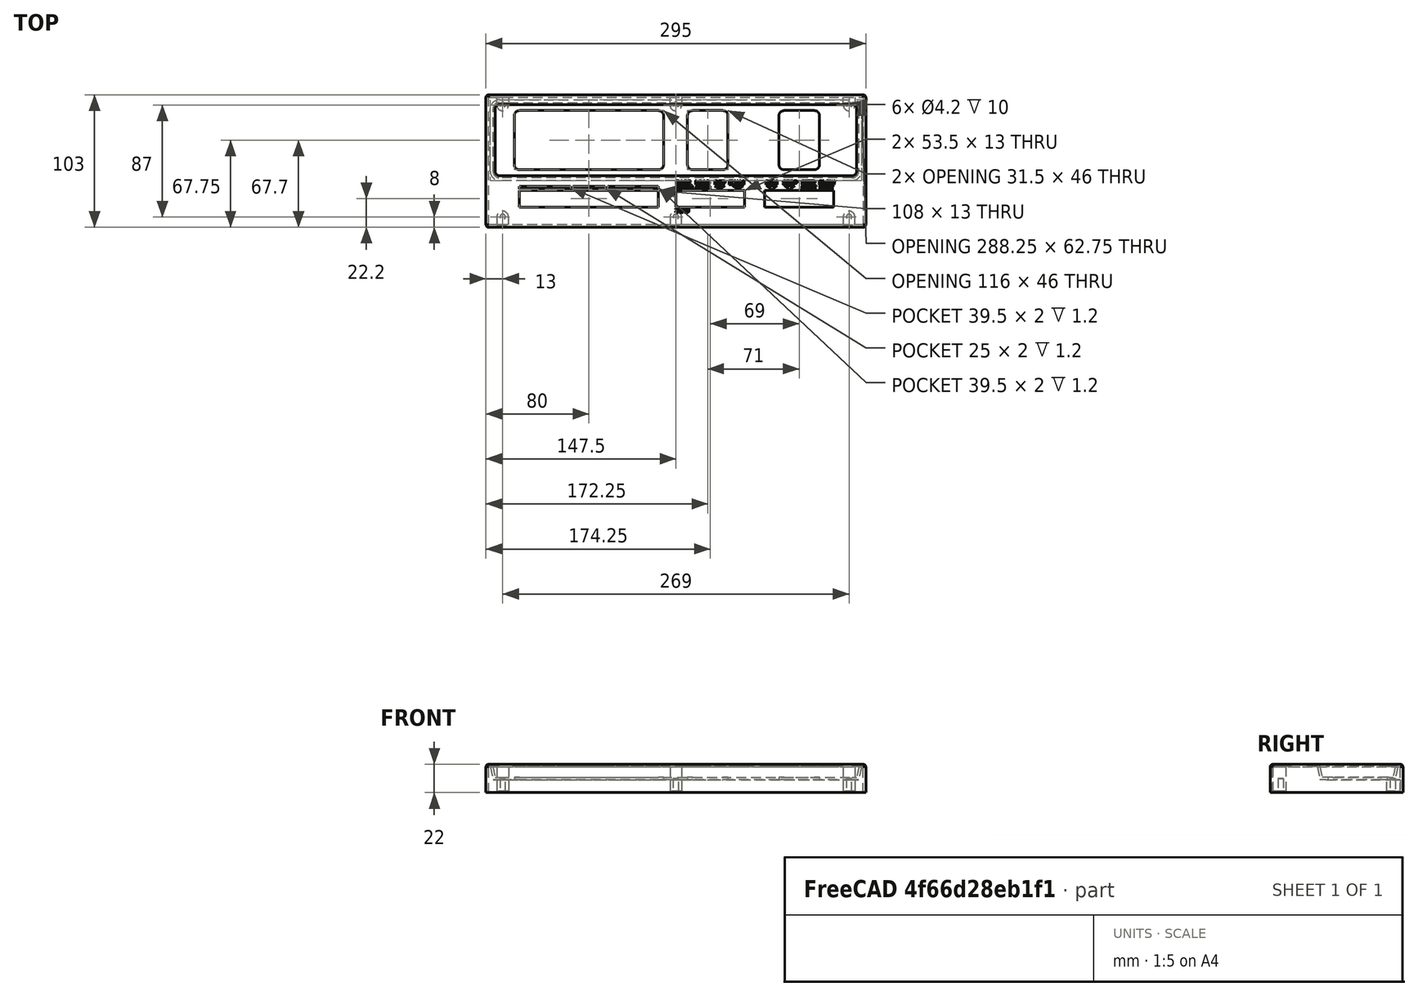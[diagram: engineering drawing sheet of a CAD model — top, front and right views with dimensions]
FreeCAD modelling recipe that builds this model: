
FCSTD DOCUMENT  (FreeCAD 1.0R39109 (Git))
Label: front panel
License: All rights reserved
LicenseURL: http://en.wikipedia.org/wiki/All_rights_reserved
objects: PartDesign::Pocket×17, Part::Part2DObjectPython×13, Sketcher::SketchObject×7, PartDesign::LinearPattern×4, PartDesign::Pad×3, PartDesign::Draft×1, PartDesign::Thickness×1, PartDesign::MultiTransform×1, PartDesign::Body×1, TechDraw::DrawSVGTemplate×1, TechDraw::DrawProjGroupItem×1, TechDraw::DrawProjGroup×1, TechDraw::DrawViewDimension×1, TechDraw::DrawPage×1, Mesh::Feature×1
note: 106 computed .brp shape members not serialized (recipe doc carries the construction recipe); baked Part::Feature solids carry a one-line shape summary decoded from their .brp

FEATURE [Sketcher::SketchObject] Sketch
  ArcFitTolerance = 0
  AttachmentSupport = -> [XY_Plane]
  FullyConstrained = true
  MakeInternals = false
  MapMode = 5
  sketch-geometry (4):
    g0: LineSegment StartX=-145.5 StartY=49.5 StartZ=0 EndX=145.5 EndY=49.5 EndZ=0
    g1: LineSegment StartX=145.5 StartY=49.5 StartZ=0 EndX=145.5 EndY=-49.5 EndZ=0
    g2: LineSegment StartX=145.5 StartY=-49.5 StartZ=0 EndX=-145.5 EndY=-49.5 EndZ=0
    g3: LineSegment StartX=-145.5 StartY=-49.5 StartZ=0 EndX=-145.5 EndY=49.5 EndZ=0
  constraints (11):
    c: Coincident(g0,g1)
    c: Coincident(g1,g2)
    c: Coincident(g2,g3)
    c: Coincident(g3,g0)
    c: Horizontal(g0)
    c: Horizontal(g2)
    c: Vertical(g1)
    c: Vertical(g3)
    c: Symmetric(g1,g0,g-1)
    c: DistanceY(g3,g3) = 99
    c: DistanceX(g0,g0) = 291
FEATURE [PartDesign::Pad] Pad
  Direction = (0,0,1)
  Length = 20
  Length2 = 10
  Profile = -> Sketch
  ReferenceAxis = -> Sketch [N_Axis]
  Suppressed = false
  Type = 0
FEATURE [Sketcher::SketchObject] Sketch001
  ArcFitTolerance = 0
  AttachmentSupport = -> [Pad]
  FullyConstrained = true
  MakeInternals = false
  MapMode = 5
  Placement = pos=(0,0,20) rot=(0,0,1;0rad)
  sketch-geometry (10):
    g0: ArcOfCircle CenterX=-137 CenterY=40.5 CenterZ=0 NormalX=0 NormalY=0 NormalZ=1 AngleXU=0 Radius=5 StartAngle=1.5708 EndAngle=3.14159
    g1: LineSegment StartX=-137 StartY=45.5 StartZ=0 EndX=137 EndY=45.5 EndZ=0
    g2: ArcOfCircle CenterX=137 CenterY=40.5 CenterZ=0 NormalX=0 NormalY=0 NormalZ=1 AngleXU=0 Radius=5 StartAngle=5e-16 EndAngle=1.5708
    g3: LineSegment StartX=142 StartY=40.5 StartZ=0 EndX=142 EndY=-8 EndZ=0
    g4: ArcOfCircle CenterX=137 CenterY=-8 CenterZ=0 NormalX=0 NormalY=0 NormalZ=1 AngleXU=0 Radius=5 StartAngle=4.71239 EndAngle=6.28319
    g5: LineSegment StartX=137 StartY=-13 StartZ=0 EndX=-137 EndY=-13 EndZ=0
    g6: ArcOfCircle CenterX=-137 CenterY=-8 CenterZ=0 NormalX=0 NormalY=0 NormalZ=1 AngleXU=0 Radius=5 StartAngle=3.14159 EndAngle=4.71239
    g7: LineSegment StartX=-142 StartY=-8 StartZ=0 EndX=-142 EndY=40.5 EndZ=0
    g8: GeomPoint [constr] X=-142 Y=45.5 Z=0
    g9: GeomPoint [constr] X=142 Y=-13 Z=0
  constraints (23):
    c: Tangent(g0,g1) = 1.5708
    c: Tangent(g1,g2) = 1.5708
    c: Tangent(g2,g3) = 1.5708
    c: Tangent(g3,g4) = 1.5708
    c: Tangent(g4,g5) = 1.5708
    c: Tangent(g5,g6) = 1.5708
    c: Tangent(g6,g7) = 1.5708
    c: Tangent(g7,g0) = 1.5708
    c: Horizontal(g1)
    c: Horizontal(g5)
    c: Vertical(g3)
    c: Vertical(g7)
    c: Equal(g2,g4)
    c: Equal(g4,g6)
    c: PointOnObject(g8,g1)
    c: PointOnObject(g8,g7)
    c: PointOnObject(g9,g3)
    c: PointOnObject(g9,g5)
    c: Diameter(g2) = 10
    c: DistanceX(g0,g2) = 284
    c: Symmetric(g0,g2,g-2)
    c: DistanceY(g-1,g0) = 45.5
    c: DistanceY(g5,g-1) = 13
FEATURE [PartDesign::Pocket] Pocket
  BaseFeature = -> Pad
  Direction = (0,0,-1)
  Length = 10
  Length2 = 5
  Profile = -> Sketch001
  ReferenceAxis = -> Sketch001 [N_Axis]
  Suppressed = false
  Type = 0
FEATURE [PartDesign::Draft] Draft
  Angle = 12
  Base = -> Pocket [Face10]
  BaseFeature = -> Pocket
  NeutralPlane = -> Pocket [Face15]
  SupportTransform = false
  Suppressed = false
FEATURE [PartDesign::Thickness] Thickness
  Base = -> Draft [Face4]
  BaseFeature = -> Draft
  Intersection = false
  Join = 0
  Mode = 0
  SupportTransform = false
  Suppressed = false
  Value = 2
FEATURE [Sketcher::SketchObject] Sketch002
  ArcFitTolerance = 0
  AttachmentSupport = -> [Thickness]
  FullyConstrained = true
  MakeInternals = false
  MapMode = 5
  Placement = pos=(0,0,22) rot=(0,0,1;0rad)
  sketch-geometry (42):
    g0: LineSegment StartX=-121.5 StartY=-22.8 StartZ=0 EndX=-13.5 EndY=-22.8 EndZ=0
    g1: LineSegment StartX=-13.5 StartY=-22.8 StartZ=0 EndX=-13.5 EndY=-35.8 EndZ=0
    g2: LineSegment StartX=-13.5 StartY=-35.8 StartZ=0 EndX=-121.5 EndY=-35.8 EndZ=0
    g3: LineSegment StartX=-121.5 StartY=-35.8 StartZ=0 EndX=-121.5 EndY=-22.8 EndZ=0
    g4: LineSegment StartX=0 StartY=-22.8 StartZ=0 EndX=53.5 EndY=-22.8 EndZ=0
    g5: LineSegment StartX=53.5 StartY=-22.8 StartZ=0 EndX=53.5 EndY=-35.8 EndZ=0
    g6: LineSegment StartX=53.5 StartY=-35.8 StartZ=0 EndX=0 EndY=-35.8 EndZ=0
    g7: LineSegment StartX=0 StartY=-35.8 StartZ=0 EndX=0 EndY=-22.8 EndZ=0
    g8: LineSegment StartX=69 StartY=-22.8 StartZ=0 EndX=122.5 EndY=-22.8 EndZ=0
    g9: LineSegment StartX=122.5 StartY=-22.8 StartZ=0 EndX=122.5 EndY=-35.8 EndZ=0
    g10: LineSegment StartX=122.5 StartY=-35.8 StartZ=0 EndX=69 EndY=-35.8 EndZ=0
    g11: LineSegment StartX=69 StartY=-35.8 StartZ=0 EndX=69 EndY=-22.8 EndZ=0
    g12: ArcOfCircle CenterX=-121.5 CenterY=35.2 CenterZ=0 NormalX=0 NormalY=0 NormalZ=1 AngleXU=0 Radius=4 StartAngle=1.5708 EndAngle=3.14159
    g13: LineSegment StartX=-121.5 StartY=39.2 StartZ=0 EndX=-13.5 EndY=39.2 EndZ=0
    g14: ArcOfCircle CenterX=-13.5 CenterY=35.2 CenterZ=0 NormalX=0 NormalY=0 NormalZ=1 AngleXU=0 Radius=4 StartAngle=-9e-16 EndAngle=1.5708
    g15: LineSegment StartX=-9.5 StartY=35.2 StartZ=0 EndX=-9.5 EndY=-2.8 EndZ=0
    g16: ArcOfCircle CenterX=-13.5 CenterY=-2.8 CenterZ=0 NormalX=0 NormalY=0 NormalZ=1 AngleXU=0 Radius=4 StartAngle=4.71239 EndAngle=6.28319
    g17: LineSegment StartX=-13.5 StartY=-6.8 StartZ=0 EndX=-121.5 EndY=-6.8 EndZ=0
    g18: ArcOfCircle CenterX=-121.5 CenterY=-2.8 CenterZ=0 NormalX=0 NormalY=0 NormalZ=1 AngleXU=0 Radius=4 StartAngle=3.14159 EndAngle=4.71239
    g19: LineSegment StartX=-125.5 StartY=-2.8 StartZ=0 EndX=-125.5 EndY=35.2 EndZ=0
    g20: GeomPoint [constr] X=-125.5 Y=39.2 Z=0
    g21: GeomPoint [constr] X=-9.5 Y=-6.8 Z=0
    g22: ArcOfCircle CenterX=13 CenterY=35.2 CenterZ=0 NormalX=0 NormalY=0 NormalZ=1 AngleXU=0 Radius=4 StartAngle=1.5708 EndAngle=3.14159
    g23: LineSegment StartX=13 StartY=39.2 StartZ=0 EndX=36.5 EndY=39.2 EndZ=0
    g24: ArcOfCircle CenterX=36.5 CenterY=35.2 CenterZ=0 NormalX=0 NormalY=0 NormalZ=1 AngleXU=0 Radius=4 StartAngle=-9e-16 EndAngle=1.5708
    g25: LineSegment StartX=40.5 StartY=35.2 StartZ=0 EndX=40.5 EndY=-2.8 EndZ=0
    g26: ArcOfCircle CenterX=36.5 CenterY=-2.8 CenterZ=0 NormalX=0 NormalY=0 NormalZ=1 AngleXU=0 Radius=4 StartAngle=4.71239 EndAngle=6.28319
    g27: LineSegment StartX=36.5 StartY=-6.8 StartZ=0 EndX=13 EndY=-6.8 EndZ=0
    g28: ArcOfCircle CenterX=13 CenterY=-2.8 CenterZ=0 NormalX=0 NormalY=0 NormalZ=1 AngleXU=0 Radius=4 StartAngle=3.14159 EndAngle=4.71239
    g29: LineSegment StartX=9 StartY=-2.8 StartZ=0 EndX=9 EndY=35.2 EndZ=0
    g30: GeomPoint [constr] X=9 Y=39.2 Z=0
    g31: GeomPoint [constr] X=40.5 Y=-6.8 Z=0
    g32: ArcOfCircle CenterX=84 CenterY=35.2 CenterZ=0 NormalX=0 NormalY=0 NormalZ=1 AngleXU=0 Radius=4 StartAngle=1.5708 EndAngle=3.14159
    g33: LineSegment StartX=84 StartY=39.2 StartZ=0 EndX=107.5 EndY=39.2 EndZ=0
    g34: ArcOfCircle CenterX=107.5 CenterY=35.2 CenterZ=0 NormalX=0 NormalY=0 NormalZ=1 AngleXU=0 Radius=4 StartAngle=0 EndAngle=1.5708
    g35: LineSegment StartX=111.5 StartY=35.2 StartZ=0 EndX=111.5 EndY=-2.8 EndZ=0
    g36: ArcOfCircle CenterX=107.5 CenterY=-2.8 CenterZ=0 NormalX=0 NormalY=0 NormalZ=1 AngleXU=0 Radius=4 StartAngle=4.71239 EndAngle=6.28319
    g37: LineSegment StartX=107.5 StartY=-6.8 StartZ=0 EndX=84 EndY=-6.8 EndZ=0
    g38: ArcOfCircle CenterX=84 CenterY=-2.8 CenterZ=0 NormalX=0 NormalY=0 NormalZ=1 AngleXU=0 Radius=4 StartAngle=3.14159 EndAngle=4.71239
    g39: LineSegment StartX=80 StartY=-2.8 StartZ=0 EndX=80 EndY=35.2 EndZ=0
    g40: GeomPoint [constr] X=80 Y=39.2 Z=0
    g41: GeomPoint [constr] X=111.5 Y=-6.8 Z=0
  constraints (108):
    c: Coincident(g0,g1)
    c: Coincident(g1,g2)
    c: Coincident(g2,g3)
    c: Coincident(g3,g0)
    c: Horizontal(g0)
    c: Horizontal(g2)
    c: Vertical(g1)
    c: Vertical(g3)
    c: Coincident(g4,g5)
    c: Coincident(g5,g6)
    c: Coincident(g6,g7)
    c: Coincident(g7,g4)
    c: Horizontal(g4)
    c: Horizontal(g6)
    c: Vertical(g5)
    c: Vertical(g7)
    c: Coincident(g8,g9)
    c: Coincident(g9,g10)
    c: Coincident(g10,g11)
    c: Coincident(g11,g8)
    c: Horizontal(g8)
    c: Horizontal(g10)
    c: Vertical(g9)
    c: Vertical(g11)
    c: Horizontal(g10,g5)
    c: Horizontal(g5,g1)
    c: Horizontal(g4,g0)
    c: Horizontal(g0,g8)
    c: DistanceY(g3,g3) = 13
    c: DistanceX(g2,g-1) = 121.5
    c: DistanceX(g0,g0) = 108
    c: DistanceY(g1,g-1) = 35.8
    c: DistanceX(g0,g4) = 13.5
    c: DistanceX(g4,g4) = 53.5
    c: DistanceX(g4,g8) = 15.5
    c: Equal(g8,g4)
    c: Tangent(g12,g13) = 1.5708
    c: Tangent(g13,g14) = 1.5708
    c: Tangent(g14,g15) = 1.5708
    c: Tangent(g15,g16) = 1.5708
    c: Tangent(g16,g17) = 1.5708
    c: Tangent(g17,g18) = 1.5708
    c: Tangent(g18,g19) = 1.5708
    c: Tangent(g19,g12) = 1.5708
    c: Horizontal(g13)
    c: Horizontal(g17)
    c: Vertical(g15)
    c: Vertical(g19)
    c: Equal(g12,g14)
    c: Equal(g14,g16)
    c: Equal(g16,g18)
    c: PointOnObject(g20,g13)
    c: PointOnObject(g20,g19)
    c: PointOnObject(g21,g15)
    c: PointOnObject(g21,g17)
    c: Radius(g12) = 4
    c: Vertical(g17,g0)
    c: Vertical(g16,g0)
    c: Tangent(g22,g23) = 1.5708
    c: Tangent(g23,g24) = 1.5708
    c: Tangent(g24,g25) = 1.5708
    c: Tangent(g25,g26) = 1.5708
    c: Tangent(g26,g27) = 1.5708
    c: Tangent(g27,g28) = 1.5708
    c: Tangent(g28,g29) = 1.5708
    c: Tangent(g29,g22) = 1.5708
    c: Horizontal(g23)
    c: Horizontal(g27)
    c: Vertical(g25)
    c: Vertical(g29)
    c: Equal(g22,g24)
    c: Equal(g24,g26)
    c: Equal(g26,g28)
    c: PointOnObject(g30,g23)
    c: PointOnObject(g30,g29)
    c: PointOnObject(g31,g25)
    c: PointOnObject(g31,g27)
    c: Equal(g26,g14)
    c: Horizontal(g22,g13)
    c: Horizontal(g27,g16)
    c: DistanceX(g26,g4) = 17
    c: DistanceX(g4,g27) = 13
    c: Tangent(g32,g33) = 1.5708
    c: Tangent(g33,g34) = 1.5708
    c: Tangent(g34,g35) = 1.5708
    c: Tangent(g35,g36) = 1.5708
    c: Tangent(g36,g37) = 1.5708
    c: Tangent(g37,g38) = 1.5708
    c: Tangent(g38,g39) = 1.5708
    c: Tangent(g39,g32) = 1.5708
    c: Horizontal(g33)
    c: Horizontal(g37)
    c: Vertical(g35)
    c: Vertical(g39)
    c: Equal(g32,g34)
    c: Equal(g34,g36)
    c: Equal(g36,g38)
    c: PointOnObject(g40,g33)
    c: PointOnObject(g40,g39)
    c: PointOnObject(g41,g35)
    c: PointOnObject(g41,g37)
    c: Horizontal(g23,g32)
    c: Equal(g32,g24)
    c: DistanceX(g36,g8) = 15
    c: DistanceY(g8,g35) = 20
    c: DistanceY(g8,g33) = 62
    c: Horizontal(g37,g16)
    c: Equal(g37,g27)
FEATURE [PartDesign::Pocket] Pocket001  label="Switch cut out"
  BaseFeature = -> Thickness
  Direction = (0,0,-1)
  Length = 5
  Length2 = 5
  Profile = -> Sketch002
  ReferenceAxis = -> Sketch002 [N_Axis]
  Suppressed = false
  Type = 1
FEATURE [Sketcher::SketchObject] Sketch003
  ArcFitTolerance = 0
  AttachmentSupport = -> [Pocket001]
  ExternalGeometry = -> [Pocket001]
  FullyConstrained = false
  MakeInternals = false
  MapMode = 5
  Placement = pos=(0,0,20) rot=(1,0,0;3.14159rad)
  sketch-geometry (5):
    g0: Circle [constr] CenterX=-134.5 CenterY=43.5 CenterZ=0 NormalX=0 NormalY=0 NormalZ=1 AngleXU=0 Radius=4.5
    g1: ArcOfCircle CenterX=-134.5 CenterY=43.5 CenterZ=0 NormalX=0 NormalY=0 NormalZ=1 AngleXU=0 Radius=4.5 StartAngle=3.14571 EndAngle=6.27841
    g2: LineSegment StartX=-139 StartY=43.4815 StartZ=0 EndX=-139.025 EndY=49.5 EndZ=0
    g3: LineSegment StartX=-139.025 StartY=49.5 StartZ=0 EndX=-130 EndY=49.5 EndZ=0
    g4: LineSegment StartX=-130 StartY=49.5 StartZ=0 EndX=-130 EndY=43.4785 EndZ=0
  constraints (12):
    c: DistanceY(g-1,g0) = 43.5
    c: DistanceX(g0,g-1) = 134.5
    c: Diameter(g0) = 9
    c: Coincident(g1,g0)
    c: PointOnObject(g1,g0)
    c: Tangent(g1,g2) = 1.5708
    c: Coincident(g2,g3)
    c: PointOnObject(g3,g-3)
    c: Horizontal(g3)
    c: Coincident(g3,g4)
    c: Coincident(g4,g1)
    c: Vertical(g4)
FEATURE [PartDesign::Pad] Pad001
  BaseFeature = -> Pocket001
  Direction = (0,0,-1)
  Length = 19
  Length2 = 10
  Profile = -> Sketch003
  ReferenceAxis = -> Sketch003 [N_Axis]
  Suppressed = false
  Type = 0
FEATURE [PartDesign::LinearPattern] LinearPattern
  BaseFeature = -> Pad001
  Direction = -> Sketch003 [H_Axis]
  Length = 269
  Mode = 0
  Occurrences = 3
  Offset = 134.5
  Originals = -> [Pad001]
  Suppressed = false
  TransformMode = 0
FEATURE [Sketcher::SketchObject] Sketch004
  ArcFitTolerance = 0
  AttachmentSupport = -> [LinearPattern]
  ExternalGeometry = -> [LinearPattern]
  FullyConstrained = true
  MakeInternals = false
  MapMode = 5
  Placement = pos=(0,0,10) rot=(1,0,0;3.14159rad)
  sketch-geometry (4):
    g0: ArcOfCircle CenterX=-134.5 CenterY=-43.5 CenterZ=0 NormalX=0 NormalY=0 NormalZ=1 AngleXU=0 Radius=4.5 StartAngle=-9e-16 EndAngle=3.14159
    g1: LineSegment StartX=-139 StartY=-43.5 StartZ=0 EndX=-139 EndY=-49.5 EndZ=0
    g2: LineSegment StartX=-139 StartY=-49.5 StartZ=0 EndX=-130 EndY=-49.5 EndZ=0
    g3: LineSegment StartX=-130 StartY=-49.5 StartZ=0 EndX=-130 EndY=-43.5 EndZ=0
  constraints (11):
    c: Tangent(g0,g1) = -1.5708
    c: Coincident(g1,g2)
    c: PointOnObject(g2,g-3)
    c: Horizontal(g2)
    c: Coincident(g2,g3)
    c: Vertical(g3)
    c: Vertical(g1)
    c: Diameter(g0) = 9
    c: DistanceX(g0,g-1) = 134.5
    c: DistanceY(g0,g-1) = 43.5
    c: Tangent(g3,g0) = -1.5708
FEATURE [PartDesign::Pad] Pad002
  BaseFeature = -> LinearPattern
  Direction = (0,0,-1)
  Length = 9
  Length2 = 10
  Profile = -> Sketch004
  ReferenceAxis = -> Sketch004 [N_Axis]
  Suppressed = false
  Type = 0
FEATURE [PartDesign::LinearPattern] LinearPattern001
  BaseFeature = -> Pad002
  Direction = -> Sketch004 [H_Axis]
  Length = 269
  Mode = 0
  Occurrences = 3
  Offset = 134.5
  Originals = -> [Pad002]
  Suppressed = false
  TransformMode = 0
FEATURE [Sketcher::SketchObject] Sketch005
  ArcFitTolerance = 0
  AttachmentSupport = -> [LinearPattern001]
  ExternalGeometry = -> [LinearPattern001]
  FullyConstrained = true
  MakeInternals = false
  MapMode = 5
  Placement = pos=(0,0,1) rot=(1,0,0;3.14159rad)
  sketch-geometry (1):
    g0: Circle CenterX=-134.5 CenterY=43.5 CenterZ=0 NormalX=0 NormalY=0 NormalZ=1 AngleXU=0 Radius=2.1
  constraints (2):
    c: Coincident(g0,g-3)
    c: Diameter(g0) = 4.2
FEATURE [PartDesign::Pocket] Pocket002
  BaseFeature = -> LinearPattern001
  Direction = (0,0,1)
  Length = 10
  Length2 = 5
  Profile = -> Sketch005
  ReferenceAxis = -> Sketch005 [N_Axis]
  Suppressed = false
  Type = 0
FEATURE [PartDesign::LinearPattern] LinearPattern002
  Direction = -> Sketch005 [H_Axis]
  Length = 269
  Mode = 0
  Occurrences = 3
  Offset = 134.5
  Suppressed = false
  TransformMode = 0
FEATURE [PartDesign::LinearPattern] LinearPattern003
  Direction = -> Sketch005 [V_Axis]
  Length = 87
  Mode = 0
  Occurrences = 2
  Offset = 87
  Reversed = true
  Suppressed = false
  TransformMode = 0
FEATURE [PartDesign::MultiTransform] MultiTransform
  BaseFeature = -> Pocket002
  Originals = -> [Pocket002]
  Suppressed = false
  TransformMode = 0
  Transformations = -> [LinearPattern002,LinearPattern003]
FEATURE [Sketcher::SketchObject] Sketch006
  ArcFitTolerance = 0
  AttachmentSupport = -> [MultiTransform]
  ExternalGeometry = -> [MultiTransform]
  FullyConstrained = true
  MakeInternals = false
  MapMode = 5
  Placement = pos=(0,0,22) rot=(0,0,1;0rad)
  sketch-geometry (28):
    g0: LineSegment StartX=-121.5 StartY=-19.8 StartZ=0 EndX=-82 EndY=-19.8 EndZ=0
    g1: LineSegment StartX=-82 StartY=-19.8 StartZ=0 EndX=-82 EndY=-21.8 EndZ=0
    g2: LineSegment StartX=-82 StartY=-21.8 StartZ=0 EndX=-121.5 EndY=-21.8 EndZ=0
    g3: LineSegment StartX=-121.5 StartY=-21.8 StartZ=0 EndX=-121.5 EndY=-19.8 EndZ=0
    g4: LineSegment StartX=-80 StartY=-19.8 StartZ=0 EndX=-55 EndY=-19.8 EndZ=0
    g5: LineSegment StartX=-55 StartY=-19.8 StartZ=0 EndX=-55 EndY=-21.8 EndZ=0
    g6: LineSegment StartX=-55 StartY=-21.8 StartZ=0 EndX=-80 EndY=-21.8 EndZ=0
    g7: LineSegment StartX=-80 StartY=-21.8 StartZ=0 EndX=-80 EndY=-19.8 EndZ=0
    g8: LineSegment StartX=-53 StartY=-19.8 StartZ=0 EndX=-13.5 EndY=-19.8 EndZ=0
    g9: LineSegment StartX=-13.5 StartY=-19.8 StartZ=0 EndX=-13.5 EndY=-21.8 EndZ=0
    g10: LineSegment StartX=-13.5 StartY=-21.8 StartZ=0 EndX=-53 EndY=-21.8 EndZ=0
    g11: LineSegment StartX=-53 StartY=-21.8 StartZ=0 EndX=-53 EndY=-19.8 EndZ=0
    g12: LineSegment StartX=52 StartY=-19.3 StartZ=0 EndX=44 EndY=-19.3 EndZ=0
    g13: LineSegment StartX=44 StartY=-19.3 StartZ=0 EndX=48 EndY=-21.8 EndZ=0
    g14: LineSegment StartX=48 StartY=-21.8 StartZ=0 EndX=52 EndY=-19.3 EndZ=0
    g15: Circle [constr] CenterX=48 CenterY=-17.35 CenterZ=0 NormalX=0 NormalY=0 NormalZ=1 AngleXU=0 Radius=4.45
    g16: LineSegment StartX=34.2 StartY=-21.8 StartZ=0 EndX=38.2 EndY=-19.3 EndZ=0
    g17: LineSegment StartX=38.2 StartY=-19.3 StartZ=0 EndX=30.2 EndY=-19.3 EndZ=0
    g18: LineSegment StartX=30.2 StartY=-19.3 StartZ=0 EndX=34.2 EndY=-21.8 EndZ=0
    g19: Circle [constr] CenterX=34.2 CenterY=-17.35 CenterZ=0 NormalX=0 NormalY=0 NormalZ=1 AngleXU=0 Radius=4.45
    g20: LineSegment StartX=74.5 StartY=-22.3 StartZ=0 EndX=78.5 EndY=-19.3 EndZ=0
    g21: LineSegment StartX=78.5 StartY=-19.3 StartZ=0 EndX=70.5 EndY=-19.3 EndZ=0
    g22: LineSegment StartX=70.5 StartY=-19.3 StartZ=0 EndX=74.5 EndY=-22.3 EndZ=0
    g23: Circle [constr] CenterX=74.5 CenterY=-18.1333 CenterZ=0 NormalX=0 NormalY=0 NormalZ=1 AngleXU=0 Radius=4.16667
    g24: LineSegment StartX=88.3 StartY=-22.3 StartZ=0 EndX=92.3 EndY=-19.3 EndZ=0
    g25: LineSegment StartX=92.3 StartY=-19.3 StartZ=0 EndX=84.3 EndY=-19.3 EndZ=0
    g26: LineSegment StartX=84.3 StartY=-19.3 StartZ=0 EndX=88.3 EndY=-22.3 EndZ=0
    g27: Circle [constr] CenterX=88.3 CenterY=-18.1333 CenterZ=0 NormalX=0 NormalY=0 NormalZ=1 AngleXU=0 Radius=4.16667
  constraints (84):
    c: Coincident(g0,g1)
    c: Coincident(g1,g2)
    c: Coincident(g2,g3)
    c: Coincident(g3,g0)
    c: Horizontal(g0)
    c: Horizontal(g2)
    c: Vertical(g1)
    c: Vertical(g3)
    c: Coincident(g4,g5)
    c: Coincident(g5,g6)
    c: Coincident(g6,g7)
    c: Coincident(g7,g4)
    c: Horizontal(g4)
    c: Horizontal(g6)
    c: Vertical(g5)
    c: Vertical(g7)
    c: Coincident(g8,g9)
    c: Coincident(g9,g10)
    c: Coincident(g10,g11)
    c: Coincident(g11,g8)
    c: Horizontal(g8)
    c: Horizontal(g10)
    c: Vertical(g9)
    c: Vertical(g11)
    c: DistanceY(g3,g3) = 2
    c: Vertical(g2,g-3)
    c: Equal(g8,g0)
    c: Horizontal(g6,g1)
    c: Horizontal(g1,g10)
    c: Horizontal(g8,g4)
    c: Horizontal(g4,g0)
    c: Vertical(g9,g-4)
    c: DistanceY(g-3,g2) = 1
    c: DistanceX(g0,g4) = 2
    c: DistanceX(g4,g8) = 2
    c: DistanceX(g8,g8) = 39.5
    c: Coincident(g12,g13)
    c: Coincident(g13,g14)
    c: Coincident(g14,g12)
    c: PointOnObject(g12,g15)
    c: PointOnObject(g13,g15)
    c: PointOnObject(g14,g15)
    c: Coincident(g16,g17)
    c: Coincident(g17,g18)
    c: Coincident(g18,g16)
    c: Equal(g16,g18)
    c: PointOnObject(g16,g19)
    c: PointOnObject(g17,g19)
    c: PointOnObject(g18,g19)
    c: Horizontal(g17)
    c: Horizontal(g12)
    c: Equal(g16,g13)
    c: DistanceX(g19,g15) = 13.8
    c: Equal(g17,g12)
    c: Horizontal(g16,g12)
    c: Equal(g14,g13)
    c: DistanceX(g17,g17) = 8
    c: DistanceY(g16,g16) = 2.5
    c: DistanceX(g13,g-5) = 5.5
    c: DistanceY(g-5,g13) = 1
    c: Coincident(g20,g21)
    c: Coincident(g21,g22)
    c: Coincident(g22,g20)
    c: Equal(g20,g22)
    c: PointOnObject(g20,g23)
    c: PointOnObject(g21,g23)
    c: PointOnObject(g22,g23)
    c: Coincident(g24,g25)
    c: Coincident(g25,g26)
    c: Coincident(g26,g24)
    c: Equal(g24,g26)
    c: PointOnObject(g24,g27)
    c: PointOnObject(g25,g27)
    c: PointOnObject(g26,g27)
    c: Horizontal(g25,g20)
    c: Horizontal(g25)
    c: Horizontal(g21)
    c: DistanceX(g23,g27) = 13.8
    c: Equal(g21,g25)
    c: Equal(g25,g12)
    c: DistanceY(g20,g20) = 3
    c: Horizontal(g24,g20)
    c: Horizontal(g12,g21)
    c: DistanceX(g-6,g20) = 5.5
FEATURE [PartDesign::Pocket] Pocket003  label="Down arrows"
  BaseFeature = -> MultiTransform
  Direction = (0,0,-1)
  Length = 1.2
  Length2 = 5
  Profile = -> Sketch006
  ReferenceAxis = -> Sketch006 [N_Axis]
  Suppressed = false
  Type = 0
FEATURE [Part::Part2DObjectPython] ShapeString  label="DEP"  # Draft 2D object (typed FeaturePython)
  FontFile = <userpath>/Downloads/roboto/Roboto-Black.ttf
  Fuse = false
  Justification = 6
  JustificationReference = 0
  KeepLeftMargin = true
  MakeFace = true
  ObliqueAngle = 0
  Placement = pos=(30,-18.5,22) rot=(0,0,1;0rad)
  ScaleToSize = false
  Size = 4
  String = DEP
  Tracking = 0
FEATURE [Part::Part2DObjectPython] ShapeString001  label="LOAD"  # Draft 2D object (typed FeaturePython)
  FontFile = <userpath>/Downloads/roboto/Roboto-Black.ttf
  Fuse = false
  Justification = 6
  JustificationReference = 0
  KeepLeftMargin = true
  MakeFace = true
  ObliqueAngle = 0
  Placement = pos=(15,-18.5,22) rot=(0,0,1;0rad)
  ScaleToSize = false
  Size = 4
  String = LOAD
  Tracking = 0
FEATURE [Part::Part2DObjectPython] ShapeString002  label="ADDR"  # Draft 2D object (typed FeaturePython)
  FontFile = <userpath>/Downloads/roboto/Roboto-Black.ttf
  Fuse = false
  Justification = 6
  JustificationReference = 0
  KeepLeftMargin = true
  MakeFace = true
  ObliqueAngle = 0
  Placement = pos=(15,-22.25,22) rot=(0.987988,-0.125405,-0.090301;0rad)
  ScaleToSize = false
  Size = 4
  String = ADDR
  Tracking = 0
FEATURE [PartDesign::Pocket] Pocket004  label="DEP Pocket"
  BaseFeature = -> Pocket003
  Direction = (0,0,-1)
  Length = 1.2
  Length2 = 5
  Profile = -> ShapeString
  ReferenceAxis = -> ShapeString [N_Axis]
  Suppressed = false
  Type = 0
FEATURE [PartDesign::Pocket] Pocket005  label="Load Pocket"
  BaseFeature = -> Pocket004
  Direction = (0,0,-1)
  Length = 1.2
  Length2 = 5
  Profile = -> ShapeString001
  ReferenceAxis = -> ShapeString001 [N_Axis]
  Suppressed = false
  Type = 0
FEATURE [PartDesign::Pocket] Pocket006  label="ADDR Pocket"
  BaseFeature = -> Pocket005
  Direction = (0,0,-1)
  Length = 1.2
  Length2 = 5
  Profile = -> ShapeString002
  ReferenceAxis = -> ShapeString002 [N_Axis]
  Suppressed = false
  Type = 0
FEATURE [Part::Part2DObjectPython] ShapeString003  label="EXAM"  # Draft 2D object (typed FeaturePython)
  FontFile = <userpath>/Downloads/roboto/Roboto-Black.ttf
  Fuse = false
  Justification = 6
  JustificationReference = 0
  KeepLeftMargin = true
  MakeFace = true
  ObliqueAngle = 0
  Placement = pos=(41,-18.5,22) rot=(0,0,1;0rad)
  ScaleToSize = false
  Size = 4
  String = EXAM
  Tracking = 0
FEATURE [PartDesign::Pocket] Pocket007
  BaseFeature = -> Pocket006
  Direction = (0,0,-1)
  Length = 1
  Length2 = 5
  Profile = -> ShapeString003
  ReferenceAxis = -> ShapeString003 [N_Axis]
  Suppressed = false
  Type = 0
FEATURE [Part::Part2DObjectPython] ShapeString004  # Draft 2D object (typed FeaturePython)
  FontFile = <userpath>/Downloads/roboto/Roboto-Black.ttf
  Fuse = false
  Justification = 6
  JustificationReference = 0
  KeepLeftMargin = true
  MakeFace = true
  ObliqueAngle = 0
  Placement = pos=(69.5,-18.5,22) rot=(0,0,1;0rad)
  ScaleToSize = false
  Size = 4
  String = RUN
  Tracking = 0
FEATURE [Part::Part2DObjectPython] ShapeString005  # Draft 2D object (typed FeaturePython)
  FontFile = <userpath>/Downloads/roboto/Roboto-Black.ttf
  Fuse = false
  Justification = 6
  JustificationReference = 0
  KeepLeftMargin = true
  MakeFace = true
  ObliqueAngle = 0
  Placement = pos=(83,-18.5,22) rot=(0,0,1;0rad)
  ScaleToSize = false
  Size = 4
  String = STOP
  Tracking = 0
FEATURE [Part::Part2DObjectPython] ShapeString006  # Draft 2D object (typed FeaturePython)
  FontFile = <userpath>/Downloads/roboto/Roboto-Black.ttf
  Fuse = false
  Justification = 6
  JustificationReference = 0
  KeepLeftMargin = true
  MakeFace = true
  ObliqueAngle = 0
  Placement = pos=(97.5,-18.5,22) rot=(0,0,1;0rad)
  ScaleToSize = false
  Size = 4
  String = STEP
  Tracking = 0
FEATURE [Part::Part2DObjectPython] ShapeString007  # Draft 2D object (typed FeaturePython)
  FontFile = <userpath>/Downloads/roboto/Roboto-Black.ttf
  Fuse = false
  Justification = 6
  JustificationReference = 0
  KeepLeftMargin = true
  MakeFace = true
  ObliqueAngle = 0
  Placement = pos=(111,-18.5,22) rot=(0,0,1;0rad)
  ScaleToSize = false
  Size = 4
  String = SLOW
  Tracking = 0
FEATURE [Part::Part2DObjectPython] ShapeString008  # Draft 2D object (typed FeaturePython)
  FontFile = <userpath>/Downloads/roboto/Roboto-Black.ttf
  Fuse = false
  Justification = 6
  JustificationReference = 0
  KeepLeftMargin = true
  MakeFace = true
  ObliqueAngle = 0
  Placement = pos=(97.5,-22.25,22) rot=(0,0,1;0rad)
  ScaleToSize = false
  Size = 4
  String = CONT
  Tracking = 0
FEATURE [Part::Part2DObjectPython] ShapeString009  label="FAST"  # Draft 2D object (typed FeaturePython)
  FontFile = <userpath>/Downloads/roboto/Roboto-Black.ttf
  Fuse = false
  Justification = 6
  JustificationReference = 0
  KeepLeftMargin = true
  MakeFace = true
  ObliqueAngle = 0
  Placement = pos=(111.5,-22.25,22) rot=(0,0,1;0rad)
  ScaleToSize = false
  Size = 4
  String = FAST
  Tracking = 0
FEATURE [PartDesign::Pocket] Pocket008  label="RUN"
  BaseFeature = -> Pocket007
  Direction = (0,0,-1)
  Length = 1.5
  Length2 = 5
  Profile = -> ShapeString004
  ReferenceAxis = -> ShapeString004 [N_Axis]
  Suppressed = false
  Type = 0
FEATURE [PartDesign::Pocket] Pocket009  label="STOP"
  BaseFeature = -> Pocket008
  Direction = (0,0,-1)
  Length = 1.2
  Length2 = 5
  Profile = -> ShapeString005
  ReferenceAxis = -> ShapeString005 [N_Axis]
  Suppressed = false
  Type = 0
FEATURE [PartDesign::Pocket] Pocket010  label="STEP"
  BaseFeature = -> Pocket009
  Direction = (0,0,-1)
  Length = 1.2
  Length2 = 5
  Profile = -> ShapeString006
  ReferenceAxis = -> ShapeString006 [N_Axis]
  Suppressed = false
  Type = 0
FEATURE [PartDesign::Pocket] Pocket011  label="SLOW"
  BaseFeature = -> Pocket010
  Direction = (0,0,-1)
  Length = 1.2
  Length2 = 5
  Profile = -> ShapeString007
  ReferenceAxis = -> ShapeString007 [N_Axis]
  Suppressed = false
  Type = 0
FEATURE [PartDesign::Pocket] Pocket012  label="CONT"
  BaseFeature = -> Pocket011
  Direction = (0,0,-1)
  Length = 1.2
  Length2 = 5
  Profile = -> ShapeString008
  ReferenceAxis = -> ShapeString008 [N_Axis]
  Suppressed = false
  Type = 0
FEATURE [PartDesign::Pocket] Pocket013  label="FAST001"
  BaseFeature = -> Pocket012
  Direction = (0,0,-1)
  Length = 1.2
  Length2 = 5
  Profile = -> ShapeString009
  ReferenceAxis = -> ShapeString009 [N_Axis]
  Suppressed = false
  Type = 0
FEATURE [Part::Part2DObjectPython] ShapeString010  # Draft 2D object (typed FeaturePython)
  FontFile = <userpath>/Downloads/roboto/Roboto-Black.ttf
  Fuse = false
  Justification = 6
  JustificationReference = 0
  KeepLeftMargin = true
  MakeFace = true
  ObliqueAngle = 0
  Placement = pos=(0,-18.5,22) rot=(0,0,1;0rad)
  ScaleToSize = false
  Size = 4
  String = PAGE
  Tracking = 0
FEATURE [Part::Part2DObjectPython] ShapeString011  # Draft 2D object (typed FeaturePython)
  FontFile = <userpath>/Downloads/roboto/Roboto-Black.ttf
  Fuse = false
  Justification = 6
  JustificationReference = 0
  KeepLeftMargin = true
  MakeFace = true
  ObliqueAngle = 0
  Placement = pos=(0,-22.25,22) rot=(0,0,1;0rad)
  ScaleToSize = false
  Size = 4
  String = NORM
  Tracking = 0
FEATURE [Part::Part2DObjectPython] ShapeString012  # Draft 2D object (typed FeaturePython)
  FontFile = <userpath>/Downloads/roboto/Roboto-Black.ttf
  Fuse = false
  Justification = 6
  JustificationReference = 0
  KeepLeftMargin = true
  MakeFace = true
  ObliqueAngle = 0
  Placement = pos=(-0.5,-40,22) rot=(0,0,1;0rad)
  ScaleToSize = false
  Size = 4
  String = ZER0
  Tracking = 0
FEATURE [PartDesign::Pocket] Pocket014  label="PAGE"
  BaseFeature = -> Pocket013
  Direction = (0,0,-1)
  Length = 1.2
  Length2 = 5
  Profile = -> ShapeString010
  ReferenceAxis = -> ShapeString010 [N_Axis]
  Suppressed = false
  Type = 0
FEATURE [PartDesign::Pocket] Pocket015  label="NORM"
  BaseFeature = -> Pocket014
  Direction = (0,0,-1)
  Length = 1.2
  Length2 = 5
  Profile = -> ShapeString011
  ReferenceAxis = -> ShapeString011 [N_Axis]
  Suppressed = false
  Type = 0
FEATURE [PartDesign::Pocket] Pocket016  label="ZERO"
  BaseFeature = -> Pocket015
  Direction = (0,0,-1)
  Length = 1.2
  Length2 = 5
  Profile = -> ShapeString012
  ReferenceAxis = -> ShapeString012 [N_Axis]
  Suppressed = false
  Type = 0
FEATURE [PartDesign::Body] Body
  AllowCompound = false
  Group = -> [Sketch,Pad,Sketch001,Pocket,Draft,Thickness,Sketch002,Pocket001,Sketch003,Pad001,LinearPattern,Sketch004,Pad002,LinearPattern001,Sketch005,Pocket002,MultiTransform,LinearPattern002,LinearPattern003,Sketch006,Pocket003,ShapeString,ShapeString001,ShapeString002,Pocket004,Pocket005,Pocket006,ShapeString003,Pocket007,ShapeString004,ShapeString005,ShapeString006,ShapeString007,ShapeString008,+13 more]
  Origin = -> Origin
  Tip = -> Pocket016
FEATURE [TechDraw::DrawSVGTemplate] Template
  EditableTexts = APPROVER_NAME=APPROVER NAME; AUTHOR_NAME=AUTHOR NAME; DATE=YYYY-MM-DD; DN=DN; DOCUMENT_TYPE=Mechanical assembly drawing; OWNER_NAME=OWNER NAME; PM=PM; PN=PN; REVISION=REV A; RIGHTS=(R) DO NOT DUPLICATE THIS DRAWING TO THIRD PARTIES WITHOUT OWNER'S PERMISSION!; SCALE=M x:x; SHEET=99 of 99; SIZE=A3; TITLELINE-1=FreeCAD; TOLERANCE=+/- ?
  Height = 297
  Orientation = 1
  Template = /Applications/FreeCAD.app/Contents/Resources/share/Mod/TechDraw/Templates/A3_Landscape_ISO7200_Pep.svg
  Width = 420
FEATURE [TechDraw::DrawProjGroupItem] ProjItem  label="Front"
  CoarseView = false
  Direction = (0,0,1)
  Focus = 100
  HardHidden = false
  IsoCount = 0
  IsoHidden = false
  IsoVisible = false
  LockPosition = true
  Perspective = false
  Rotation = 0
  RotationVector = (1,0,0)
  ScaleType = 2
  ScrubCount = 0
  SeamHidden = false
  SeamVisible = true
  SmoothHidden = false
  SmoothVisible = true
  Source = -> [Body]
  Type = 0
  X = 0
  XDirection = (1,0,0)
  Y = 0
FEATURE [TechDraw::DrawProjGroup] ProjGroup
  Anchor = -> ProjItem
  AutoDistribute = true
  LockPosition = false
  ProjectionType = 0
  Rotation = 0
  ScaleType = 0
  Source = -> [Body]
  Views = -> [ProjItem]
  X = 210
  Y = 148.5
  spacingX = 15
  spacingY = 15
FEATURE [TechDraw::DrawViewDimension] Dimension
  AngleOverride = false
  Arbitrary = false
  ArbitraryTolerances = false
  EqualTolerance = true
  ExtensionAngle = 0
  FormatSpec = %.3f
  FormatSpecOverTolerance = %+.3f
  FormatSpecUnderTolerance = %+.3f
  Inverted = false
  LineAngle = 0
  LockPosition = false
  MeasureType = 1
  OverTolerance = 0
  References2D = -> [ProjItem]
  Rotation = 0
  ScaleType = 0
  TheoreticalExact = false
  Type = 2
  UnderTolerance = 0
  X = 178.048
  Y = 18.5194
FEATURE [TechDraw::DrawPage] Page
  KeepUpdated = true
  NextBalloonIndex = 1
  ProjectionType = 0
  Template = -> Template
  Views = -> [ProjGroup,Dimension]
FEATURE [Mesh::Feature] Mesh  label="Body (Meshed)"
